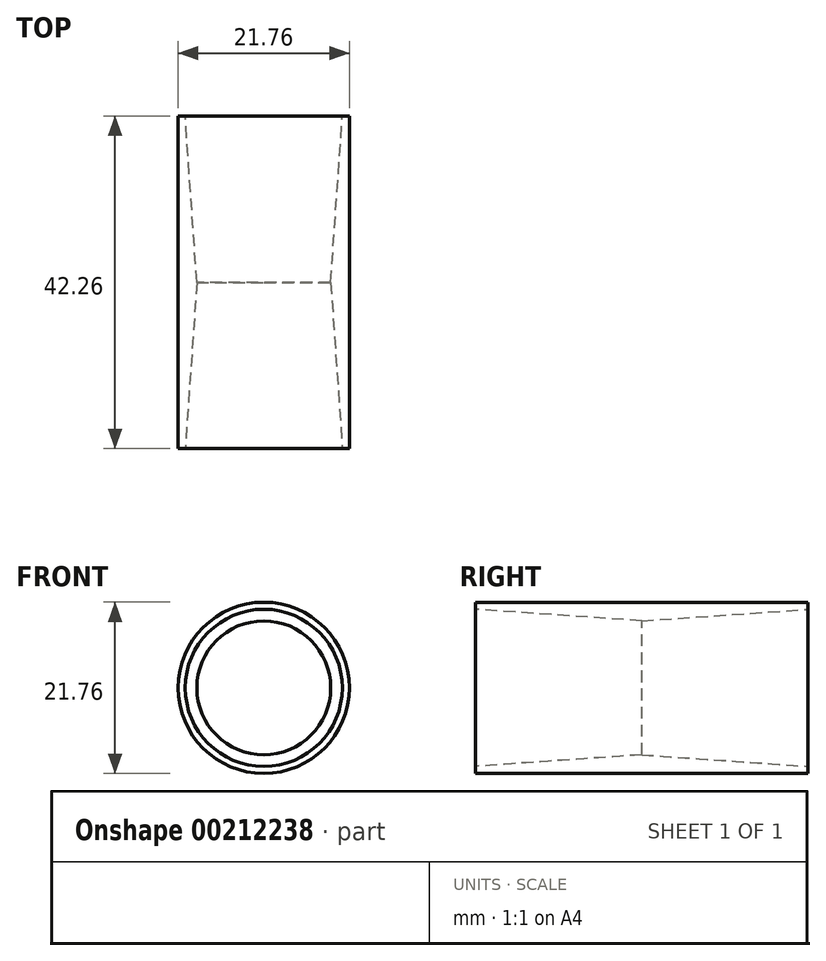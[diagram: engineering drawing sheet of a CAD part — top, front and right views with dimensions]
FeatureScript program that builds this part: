
annotation { "Feature Type Name" : "Feature", "Feature Type Description" : "" }
export const myFeature = defineFeature(function(context is Context, id is Id, definition is map)
    precondition{}
    {
        {
            var Q0;
            Q0=qCreatedBy(makeId("Front.planeOp"),FACE);
            var sketch = newSketch(context, id + "F0", { "sketchPlane" : qUnion([Q0])});
            skCircle(sketch, "E0", {"center": v(0, 0) * mm, "radius": 10.88 * mm});
            skCircle(sketch, "E1", {"center": v(0, 0) * mm, "radius": 8.5 * mm});
            skSolve(sketch);
        }
        {
            var Q0;
            Q0 = qSketchRegion(id + "F0", true);
            extrude(context, id + "F1", {"entities" : qUnion([Q0]), "endBound" : BoundingType.SYMMETRIC, "depth" : 42.25 * mm});
        }
        {
            var Q0;
            Q0=makeQuery(id+"F0.imprint","IMPRINT",FACE,{"disambiguationData":[TD([[makeQuery(id+"F0.imprint","IMPRINT",EDGE,{"derivedFrom":sQuery(id+"F0.wireOp",EDGE,"E1")}),1.0]])]});
            extrude(context, id + "F2", {"entities" : qUnion([Q0]), "operationType" : NewBodyOperationType.REMOVE, "endBound" : BoundingType.SYMMETRIC, "depth" : 42.25 * mm, "hasDraft" : true, "draftAngle" : 4 * degree});
        }
    });
